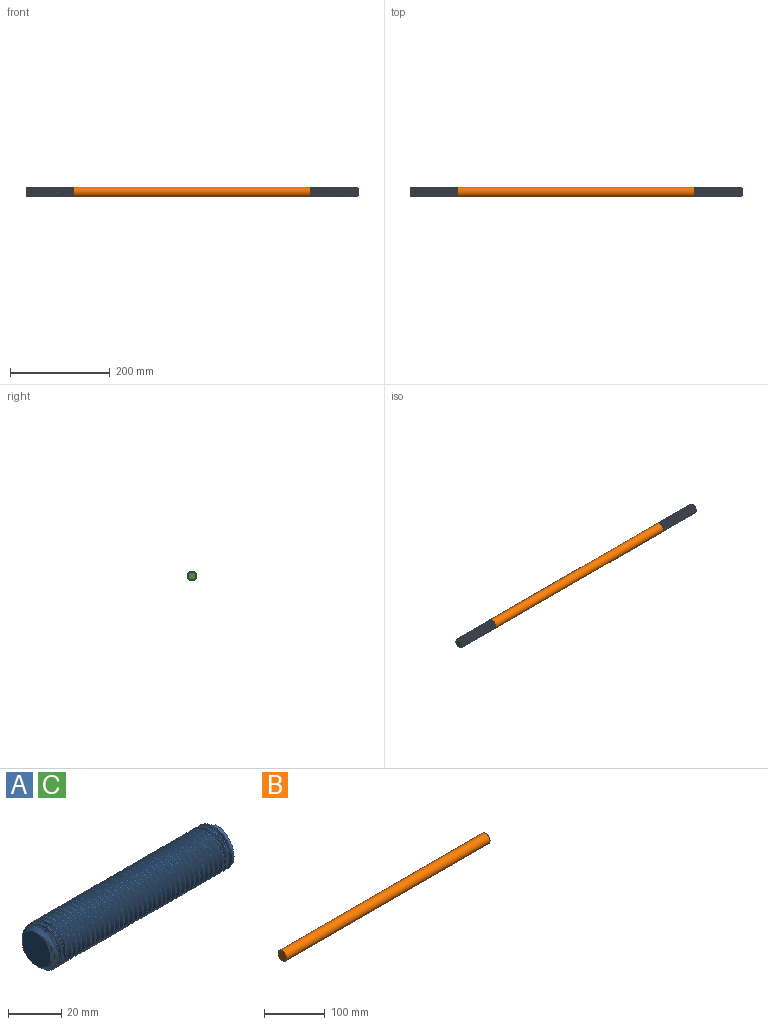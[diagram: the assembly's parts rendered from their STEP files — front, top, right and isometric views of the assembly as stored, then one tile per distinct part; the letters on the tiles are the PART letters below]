
ASSEMBLY  parts=3 mates=1
PART A: 7 faces, bbox 98.6x23.6x20.6 mm
  f0: cylinder r=9.6mm len=93mm, axis (1,0,0), area -450.6mm2, adj f2,f3,f4,f5,f6
  f1: plane 15.2x15.2mm, normal (-1,0,0), area 181.5mm2, adj f3
  f2: plane 20.59x19.82mm, normal (1,0,0), area 266.1mm2, adj f0,f4,f5
  f3: cone r=9.6mm half-angle=45deg, axis (1,0,0), area 86.9mm2, adj f0,f1,f5,f6
  f4: plane 1.89x1.09mm, normal (0,1,0), area 1mm2, adj f0,f2,f6
  f5: bspline ~96.09x22.17mm, area 4468.2mm2, adj f0,f2,f3,f6
  f6: bspline ~96.09x22.17mm, area 4445mm2, adj f0,f3,f4,f5
PART B: 3 faces, bbox 475x20x20 mm
  f0: cylinder r=10mm len=475mm, axis (-1,0,0), area 29845.1mm2, adj f1,f2
  f1: plane 20x20mm, normal (1,0,0), area 314.2mm2, adj f0
  f2: plane 20x20mm, normal (-1,0,0), area 314.2mm2, adj f0
PART C: same geometry as A
PLACE A rot(axis=(0,1,0),180deg) t=(597.99,7.81,-53.54)mm
PLACE B t=(122.99,7.81,-53.54)mm
PLACE C t=(122.99,7.81,-53.54)mm
MATE fastened A.f0 <-> B.f0  axis (-1,0,0) through (597.99,7.81,-53.54)mm
